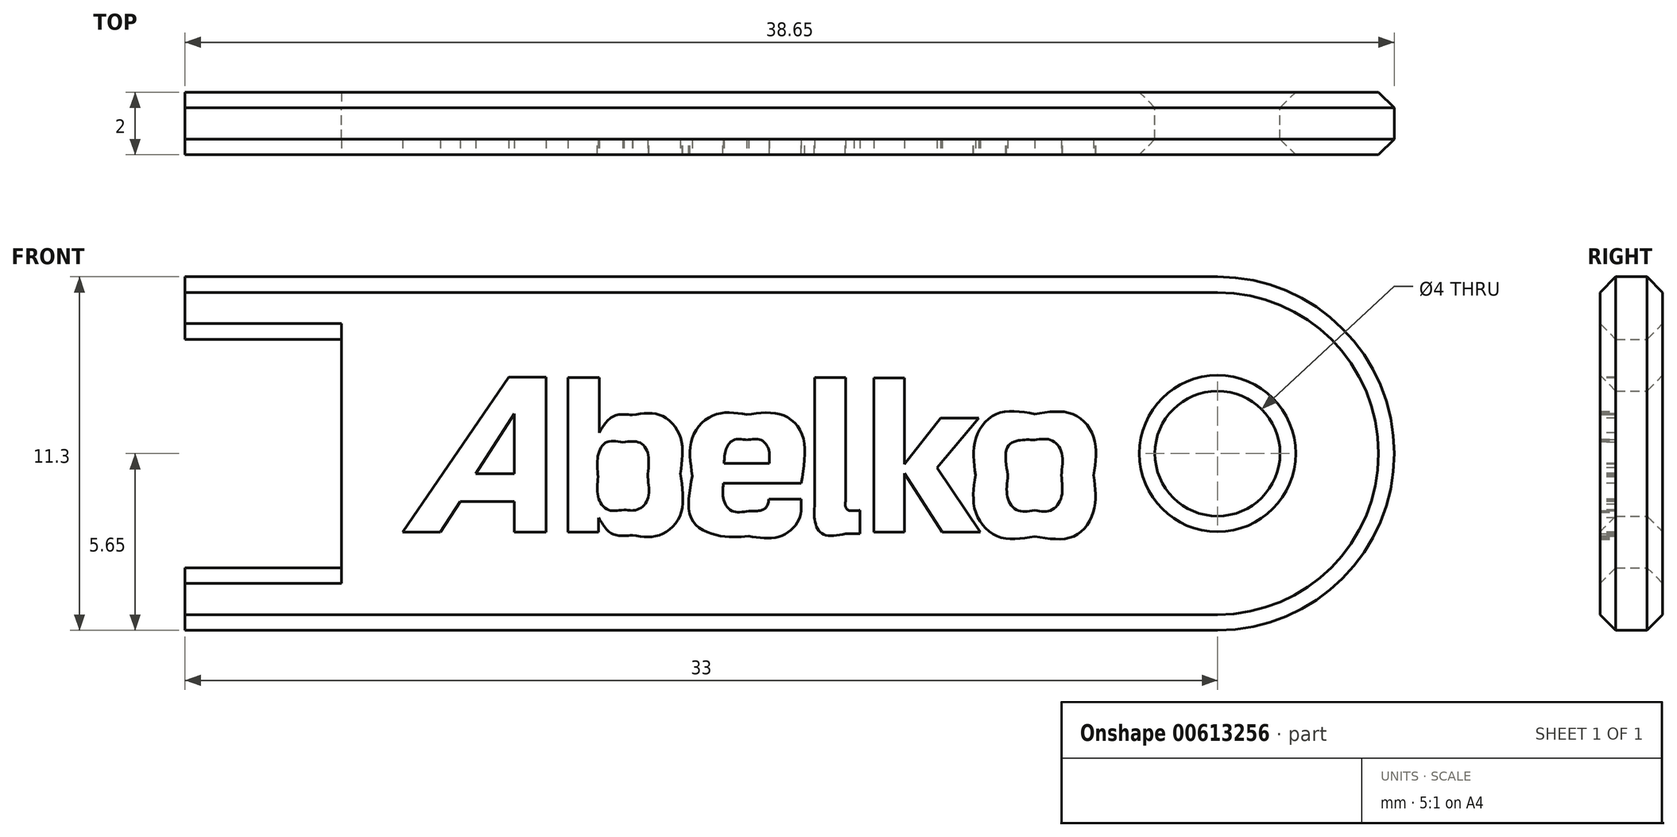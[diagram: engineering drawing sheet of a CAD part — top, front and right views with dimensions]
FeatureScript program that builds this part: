
annotation { "Feature Type Name" : "Feature", "Feature Type Description" : "" }
export const myFeature = defineFeature(function(context is Context, id is Id, definition is map)
    precondition{}
    {
        {
            var Q0;
            Q0=qCreatedBy(makeId("Front.planeOp"),FACE);
            var sketch = newSketch(context, id + "F0", { "sketchPlane" : qUnion([Q0])});
            skLineSegment(sketch, "E0", {"start": v(-13, 5.15) * mm, "end": v(-18, 5.15) * mm});
            skLineSegment(sketch, "E1", {"start": v(-18, 5.15) * mm, "end": v(-18, 7.15) * mm});
            skLineSegment(sketch, "E2", {"start": v(-18, 7.15) * mm, "end": v(15, 7.15) * mm});
            skLineSegment(sketch, "E3.MirrorCS", {"start": v(-18, -4.15) * mm, "end": v(15, -4.15) * mm});
            skLineSegment(sketch, "E4.MirrorCS", {"start": v(-18, -2.15) * mm, "end": v(-18, -4.15) * mm});
            skLineSegment(sketch, "E5.MirrorCS", {"start": v(-13, -2.15) * mm, "end": v(-18, -2.15) * mm});
            skArc(sketch, "E6", {"start": v(15, -4.15) * mm, "mid": v(20.65, 1.5) * mm, "end": v(15, 7.15) * mm});
            skLineSegment(sketch, "E7", {"start": v(-13, 5.15) * mm, "end": v(-13, -2.15) * mm});
            skLineSegment(sketch, "E8", {"start": v(-27.45, -20) * mm, "end": v(40.17, -20) * mm, "construction": true});
            skLineSegment(sketch, "E9", {"start": v(20.65, 1.5) * mm, "end": v(-13, 1.5) * mm, "construction": true});
            skCircle(sketch, "E10", {"center": v(15, 1.5) * mm, "radius": 2 * mm});
            skSolve(sketch);
        }
        {
            var Q0;
            Q0=makeQuery(id+"F0.imprint","IMPRINT",FACE,{"disambiguationData":[TD([[makeQuery(id+"F0.imprint","IMPRINT",EDGE,{"derivedFrom":sQuery(id+"F0.wireOp",EDGE,"akVr4v8H-JdDk-4HSe-9A5j-kgtD8AmrJHMh")}),-1.0]])]});
            var Q1;
            Q1=makeQuery(id+"F0.imprint","IMPRINT",FACE,{"disambiguationData":[TD([[makeQuery(id+"F0.imprint","IMPRINT",EDGE,{"derivedFrom":sQuery(id+"F0.wireOp",EDGE,"E0")}),-1.0]])]});
            extrude(context, id + "F1", {"entities" : qUnion([Q0, Q1]), "depth" : 2 * mm, "offsetDistance" : 25 * mm});
        }
        {
            var Q0;
            Q0=makeQuery(id+"F1.opExtrude","CAP_FACE",FACE,{"disambiguationData":[OSD([sQuery(id+"F0.wireOp",EDGE,"akVr4v8H-JdDk-4HSe-9A5j-kgtD8AmrJHMh"),sQuery(id+"F0.wireOp",EDGE,"E0"),sQuery(id+"F0.wireOp",EDGE,"E1"),sQuery(id+"F0.wireOp",EDGE,"E2"),sQuery(id+"F0.wireOp",EDGE,"ee2b3b4e-261e-4f05-bfb9-8a08e86599b6"),sQuery(id+"F0.wireOp",EDGE,"E3.MirrorCS"),sQuery(id+"F0.wireOp",EDGE,"26adf2fc-d08f-4d16-b653-455f8057de741.MirrorCS"),sQuery(id+"F0.wireOp",EDGE,"26adf2fc-d08f-4d16-b653-455f8057de742.MirrorCS"),sQuery(id+"F0.wireOp",EDGE,"E4.MirrorCS"),sQuery(id+"F0.wireOp",EDGE,"E5.MirrorCS")])],"isStart":false});
            var sketch = newSketch(context, id + "F2", { "sketchPlane" : qUnion([Q0])});
            skLineSegment(sketch, "E11", {"start": v(-8.71, 0.85) * mm, "end": v(-7.48, 0.85) * mm});
            skLineSegment(sketch, "E12", {"start": v(-7.48, 0.85) * mm, "end": v(-7.48, 2.77) * mm});
            skLineSegment(sketch, "E13", {"start": v(-7.48, 2.77) * mm, "end": v(-8.71, 0.85) * mm});
            skFitSpline(sketch, "E14", {"points": [v(-3.97, -0.3) * mm, v(-3.55, -0.3) * mm, v(-3.22, 0.04) * mm, v(-3.22, 0.75) * mm]});
            skFitSpline(sketch, "E15", {"points": [v(-3.22, 0.75) * mm, v(-3.22, 1.53) * mm, v(-3.5, 1.86) * mm, v(-4, 1.86) * mm]});
            skFitSpline(sketch, "E16", {"points": [v(-4, 1.86) * mm, v(-4.54, 1.86) * mm, v(-4.8, 1.45) * mm, v(-4.8, 0.76) * mm]});
            skFitSpline(sketch, "E17", {"points": [v(-4.8, 0.76) * mm, v(-4.8, 0.11) * mm, v(-4.49, -0.3) * mm, v(-3.97, -0.3) * mm]});
            skLineSegment(sketch, "E18", {"start": v(-6.46, 3.94) * mm, "end": v(-6.46, -1) * mm});
            skLineSegment(sketch, "E19", {"start": v(-6.46, -1) * mm, "end": v(-7.48, -1) * mm});
            skLineSegment(sketch, "E20", {"start": v(-7.48, -1) * mm, "end": v(-7.48, -0.04) * mm});
            skLineSegment(sketch, "E21", {"start": v(-7.48, -0.04) * mm, "end": v(-9.2, -0.04) * mm});
            skLineSegment(sketch, "E22", {"start": v(-9.2, -0.04) * mm, "end": v(-9.84, -1) * mm});
            skLineSegment(sketch, "E23", {"start": v(-9.84, -1) * mm, "end": v(-11.04, -1) * mm});
            skLineSegment(sketch, "E24", {"start": v(-11.04, -1) * mm, "end": v(-7.65, 3.94) * mm});
            skLineSegment(sketch, "E25", {"start": v(-7.65, 3.94) * mm, "end": v(-6.46, 3.94) * mm});
            skFitSpline(sketch, "E26", {"points": [v(-4.76, 2.17) * mm, v(-4.52, 2.52) * mm, v(-4.2, 2.73) * mm, v(-3.71, 2.73) * mm]});
            skFitSpline(sketch, "E27", {"points": [v(-3.71, 2.73) * mm, v(-2.82, 2.73) * mm, v(-2.17, 2.04) * mm, v(-2.17, 0.86) * mm]});
            skFitSpline(sketch, "E28", {"points": [v(-2.17, 0.86) * mm, v(-2.17, -0.47) * mm, v(-2.85, -1.11) * mm, v(-3.7, -1.11) * mm]});
            skFitSpline(sketch, "E29", {"points": [v(-3.7, -1.11) * mm, v(-4.2, -1.11) * mm, v(-4.48, -0.97) * mm, v(-4.78, -0.56) * mm]});
            skLineSegment(sketch, "E30", {"start": v(-4.76, 3.93) * mm, "end": v(-4.76, 2.17) * mm});
            skFitSpline(sketch, "E31", {"points": [v(0.67, 1.2) * mm, v(0.65, 1.64) * mm, v(0.4, 1.93) * mm, v(-0.05, 1.93) * mm]});
            skFitSpline(sketch, "E32", {"points": [v(-0.05, 1.93) * mm, v(-0.47, 1.93) * mm, v(-0.7, 1.65) * mm, v(-0.77, 1.2) * mm]});
            skLineSegment(sketch, "E33", {"start": v(-4.78, -0.56) * mm, "end": v(-4.78, -1.02) * mm});
            skLineSegment(sketch, "E34", {"start": v(-4.78, -1.02) * mm, "end": v(-5.76, -1.02) * mm});
            skLineSegment(sketch, "E35", {"start": v(-5.76, -1.02) * mm, "end": v(-5.76, 3.93) * mm});
            skLineSegment(sketch, "E36", {"start": v(-5.76, 3.93) * mm, "end": v(-4.76, 3.93) * mm});
            skFitSpline(sketch, "E37", {"points": [v(-0.05, 2.74) * mm, v(1.05, 2.74) * mm, v(1.74, 2.08) * mm, v(1.7, 0.54) * mm]});
            skLineSegment(sketch, "E38", {"start": v(-0.77, 1.2) * mm, "end": v(0.67, 1.2) * mm});
            skFitSpline(sketch, "E39", {"points": [v(-0.8, 0.54) * mm, v(-0.79, 0.04) * mm, v(-0.52, -0.34) * mm, v(0.02, -0.34) * mm]});
            skFitSpline(sketch, "E40", {"points": [v(0.02, -0.34) * mm, v(0.27, -0.34) * mm, v(0.55, -0.25) * mm, v(0.66, 0.04) * mm]});
            skLineSegment(sketch, "E41", {"start": v(1.7, 0.54) * mm, "end": v(-0.8, 0.54) * mm});
            skFitSpline(sketch, "E42", {"points": [v(1.69, 0.04) * mm, v(1.63, -0.6) * mm, v(1.03, -1.14) * mm, v(0, -1.14) * mm]});
            skFitSpline(sketch, "E43", {"points": [v(0, -1.14) * mm, v(-0.84, -1.14) * mm, v(-1.79, -0.64) * mm, v(-1.79, 0.78) * mm]});
            skFitSpline(sketch, "E44", {"points": [v(-1.79, 0.78) * mm, v(-1.79, 2.02) * mm, v(-1.06, 2.74) * mm, v(-0.05, 2.74) * mm]});
            skFitSpline(sketch, "E45", {"points": [v(3.38, -0.32) * mm, v(3.44, -0.32) * mm, v(3.53, -0.32) * mm, v(3.57, -0.32) * mm]});
            skLineSegment(sketch, "E46", {"start": v(0.66, 0.04) * mm, "end": v(1.69, 0.04) * mm});
            skFitSpline(sketch, "E47", {"points": [v(3.57, -1.06) * mm, v(3.42, -1.06) * mm, v(3.27, -1.06) * mm, v(3.12, -1.06) * mm]});
            skFitSpline(sketch, "E48", {"points": [v(3.12, -1.06) * mm, v(2.37, -1.06) * mm, v(2.12, -0.62) * mm, v(2.12, -0.12) * mm]});
            skLineSegment(sketch, "E49", {"start": v(3.57, -0.32) * mm, "end": v(3.57, -1.06) * mm});
            skFitSpline(sketch, "E50", {"points": [v(3.12, 0.02) * mm, v(3.12, -0.21) * mm, v(3.22, -0.32) * mm, v(3.38, -0.32) * mm]});
            skLineSegment(sketch, "E51", {"start": v(2.12, -0.12) * mm, "end": v(2.12, 3.93) * mm});
            skLineSegment(sketch, "E52", {"start": v(2.12, 3.93) * mm, "end": v(3.12, 3.93) * mm});
            skLineSegment(sketch, "E53", {"start": v(3.12, 3.93) * mm, "end": v(3.12, 0.02) * mm});
            skFitSpline(sketch, "E54", {"points": [v(9.15, -0.32) * mm, v(9.68, -0.32) * mm, v(10, 0.1) * mm, v(10, 0.8) * mm]});
            skFitSpline(sketch, "E55", {"points": [v(10, 0.8) * mm, v(10, 1.56) * mm, v(9.66, 1.93) * mm, v(9.15, 1.93) * mm]});
            skFitSpline(sketch, "E56", {"points": [v(9.15, 1.93) * mm, v(8.75, 1.93) * mm, v(8.3, 1.73) * mm, v(8.3, 0.81) * mm]});
            skFitSpline(sketch, "E57", {"points": [v(8.3, 0.81) * mm, v(8.3, 0.06) * mm, v(8.62, -0.32) * mm, v(9.15, -0.32) * mm]});
            skLineSegment(sketch, "E58", {"start": v(4.99, 3.91) * mm, "end": v(4.99, 1.16) * mm});
            skLineSegment(sketch, "E59", {"start": v(4.99, 1.16) * mm, "end": v(6.15, 2.63) * mm});
            skLineSegment(sketch, "E60", {"start": v(6.15, 2.63) * mm, "end": v(7.37, 2.63) * mm});
            skLineSegment(sketch, "E61", {"start": v(7.37, 2.63) * mm, "end": v(6.04, 1.04) * mm});
            skLineSegment(sketch, "E62", {"start": v(6.04, 1.04) * mm, "end": v(7.42, -1.02) * mm});
            skLineSegment(sketch, "E63", {"start": v(7.42, -1.02) * mm, "end": v(6.2, -1.02) * mm});
            skLineSegment(sketch, "E64", {"start": v(6.2, -1.02) * mm, "end": v(4.99, 0.87) * mm});
            skLineSegment(sketch, "E65", {"start": v(4.99, 0.87) * mm, "end": v(4.99, -1.02) * mm});
            skLineSegment(sketch, "E66", {"start": v(4.99, -1.02) * mm, "end": v(4.01, -1.02) * mm});
            skLineSegment(sketch, "E67", {"start": v(4.01, -1.02) * mm, "end": v(4.01, 3.91) * mm});
            skLineSegment(sketch, "E68", {"start": v(4.01, 3.91) * mm, "end": v(4.99, 3.91) * mm});
            skFitSpline(sketch, "E69", {"points": [v(9.15, 2.77) * mm, v(10.36, 2.77) * mm, v(11.04, 2) * mm, v(11.04, 0.8) * mm]});
            skFitSpline(sketch, "E70", {"points": [v(11.04, 0.8) * mm, v(11.04, -0.32) * mm, v(10.4, -1.15) * mm, v(9.16, -1.15) * mm]});
            skFitSpline(sketch, "E71", {"points": [v(9.16, -1.15) * mm, v(7.97, -1.15) * mm, v(7.26, -0.35) * mm, v(7.26, 0.81) * mm]});
            skFitSpline(sketch, "E72", {"points": [v(7.26, 0.81) * mm, v(7.26, 1.94) * mm, v(7.93, 2.77) * mm, v(9.15, 2.77) * mm]});
            skLineSegment(sketch, "E73", {"start": v(-6, -3.9) * mm, "end": v(-5.71, -3.9) * mm});
            skLineSegment(sketch, "E74", {"start": v(-5.71, -3.9) * mm, "end": v(-5.71, -2.37) * mm});
            skLineSegment(sketch, "E75", {"start": v(-5.71, -2.37) * mm, "end": v(-6, -2.37) * mm});
            skLineSegment(sketch, "E76", {"start": v(-6, -2.37) * mm, "end": v(-6, -3.9) * mm});
            skLineSegment(sketch, "E77", {"start": v(-4.47, -2.37) * mm, "end": v(-4.19, -2.37) * mm});
            skLineSegment(sketch, "E78", {"start": v(-4.19, -2.37) * mm, "end": v(-4.19, -3.9) * mm});
            skLineSegment(sketch, "E79", {"start": v(-4.19, -3.9) * mm, "end": v(-4.44, -3.9) * mm});
            skLineSegment(sketch, "E80", {"start": v(-4.44, -3.9) * mm, "end": v(-5.11, -2.83) * mm});
            skLineSegment(sketch, "E81", {"start": v(-5.11, -2.83) * mm, "end": v(-5.1, -3.9) * mm});
            skLineSegment(sketch, "E82", {"start": v(-5.1, -3.9) * mm, "end": v(-5.38, -3.9) * mm});
            skLineSegment(sketch, "E83", {"start": v(-5.38, -3.9) * mm, "end": v(-5.38, -2.37) * mm});
            skLineSegment(sketch, "E84", {"start": v(-5.38, -2.37) * mm, "end": v(-5.12, -2.37) * mm});
            skLineSegment(sketch, "E85", {"start": v(-5.12, -2.37) * mm, "end": v(-4.44, -3.45) * mm});
            skLineSegment(sketch, "E86", {"start": v(-4.44, -3.45) * mm, "end": v(-4.47, -2.37) * mm});
            skFitSpline(sketch, "E87", {"points": [v(-1.65, -2.6) * mm, v(-1.92, -2.6) * mm, v(-2.1, -2.8) * mm, v(-2.1, -3.12) * mm]});
            skFitSpline(sketch, "E88", {"points": [v(-2.1, -3.12) * mm, v(-2.1, -3.47) * mm, v(-1.9, -3.68) * mm, v(-1.65, -3.68) * mm]});
            skFitSpline(sketch, "E89", {"points": [v(-1.65, -3.68) * mm, v(-1.45, -3.68) * mm, v(-1.2, -3.54) * mm, v(-1.2, -3.17) * mm]});
            skFitSpline(sketch, "E90", {"points": [v(-1.2, -3.17) * mm, v(-1.2, -2.87) * mm, v(-1.35, -2.6) * mm, v(-1.65, -2.6) * mm]});
            skLineSegment(sketch, "E91", {"start": v(-2.94, -2.37) * mm, "end": v(-2.66, -2.37) * mm});
            skLineSegment(sketch, "E92", {"start": v(-2.66, -2.37) * mm, "end": v(-2.66, -3.9) * mm});
            skLineSegment(sketch, "E93", {"start": v(-2.66, -3.9) * mm, "end": v(-2.9, -3.9) * mm});
            skLineSegment(sketch, "E94", {"start": v(-2.9, -3.9) * mm, "end": v(-3.58, -2.83) * mm});
            skLineSegment(sketch, "E95", {"start": v(-3.58, -2.83) * mm, "end": v(-3.56, -3.9) * mm});
            skLineSegment(sketch, "E96", {"start": v(-3.56, -3.9) * mm, "end": v(-3.85, -3.9) * mm});
            skLineSegment(sketch, "E97", {"start": v(-3.85, -3.9) * mm, "end": v(-3.85, -2.37) * mm});
            skLineSegment(sketch, "E98", {"start": v(-3.85, -2.37) * mm, "end": v(-3.59, -2.37) * mm});
            skLineSegment(sketch, "E99", {"start": v(-3.59, -2.37) * mm, "end": v(-2.9, -3.45) * mm});
            skLineSegment(sketch, "E100", {"start": v(-2.9, -3.45) * mm, "end": v(-2.94, -2.37) * mm});
            skFitSpline(sketch, "E101", {"points": [v(-1.65, -3.94) * mm, v(-1.85, -3.94) * mm, v(-2.03, -3.89) * mm, v(-2.18, -3.7) * mm]});
            skFitSpline(sketch, "E102", {"points": [v(-2.18, -3.7) * mm, v(-2.34, -3.53) * mm, v(-2.39, -3.33) * mm, v(-2.39, -3.14) * mm]});
            skFitSpline(sketch, "E103", {"points": [v(-2.39, -3.14) * mm, v(-2.39, -2.67) * mm, v(-2.07, -2.33) * mm, v(-1.65, -2.33) * mm]});
            skFitSpline(sketch, "E104", {"points": [v(-1.65, -2.33) * mm, v(-1.27, -2.33) * mm, v(-0.91, -2.61) * mm, v(-0.91, -3.14) * mm]});
            skFitSpline(sketch, "E105", {"points": [v(-0.91, -3.14) * mm, v(-0.92, -3.58) * mm, v(-1.18, -3.94) * mm, v(-1.65, -3.94) * mm]});
            skLineSegment(sketch, "E106", {"start": v(0.44, -2.37) * mm, "end": v(0, -3.9) * mm});
            skLineSegment(sketch, "E107", {"start": v(0, -3.9) * mm, "end": v(-0.39, -3.9) * mm});
            skLineSegment(sketch, "E108", {"start": v(-0.39, -3.9) * mm, "end": v(-0.84, -2.37) * mm});
            skLineSegment(sketch, "E109", {"start": v(-0.84, -2.37) * mm, "end": v(-0.54, -2.37) * mm});
            skLineSegment(sketch, "E110", {"start": v(-0.54, -2.37) * mm, "end": v(-0.2, -3.58) * mm});
            skLineSegment(sketch, "E111", {"start": v(-0.2, -3.58) * mm, "end": v(0.14, -2.37) * mm});
            skLineSegment(sketch, "E112", {"start": v(0.14, -2.37) * mm, "end": v(0.44, -2.37) * mm});
            skLineSegment(sketch, "E113", {"start": v(1.28, -3.35) * mm, "end": v(1.07, -2.65) * mm});
            skLineSegment(sketch, "E114", {"start": v(1.07, -2.65) * mm, "end": v(0.86, -3.35) * mm});
            skLineSegment(sketch, "E115", {"start": v(0.86, -3.35) * mm, "end": v(1.28, -3.35) * mm});
            skLineSegment(sketch, "E116", {"start": v(1.36, -3.6) * mm, "end": v(0.78, -3.6) * mm});
            skLineSegment(sketch, "E117", {"start": v(0.78, -3.6) * mm, "end": v(0.7, -3.9) * mm});
            skLineSegment(sketch, "E118", {"start": v(0.7, -3.9) * mm, "end": v(0.38, -3.9) * mm});
            skLineSegment(sketch, "E119", {"start": v(0.38, -3.9) * mm, "end": v(0.9, -2.37) * mm});
            skLineSegment(sketch, "E120", {"start": v(0.9, -2.37) * mm, "end": v(1.23, -2.37) * mm});
            skLineSegment(sketch, "E121", {"start": v(1.23, -2.37) * mm, "end": v(1.75, -3.9) * mm});
            skLineSegment(sketch, "E122", {"start": v(1.75, -3.9) * mm, "end": v(1.45, -3.9) * mm});
            skLineSegment(sketch, "E123", {"start": v(1.45, -3.9) * mm, "end": v(1.36, -3.6) * mm});
            skLineSegment(sketch, "E124", {"start": v(2.78, -2.63) * mm, "end": v(2.35, -2.63) * mm});
            skLineSegment(sketch, "E125", {"start": v(2.35, -2.63) * mm, "end": v(2.35, -3.9) * mm});
            skLineSegment(sketch, "E126", {"start": v(2.35, -3.9) * mm, "end": v(2.06, -3.9) * mm});
            skLineSegment(sketch, "E127", {"start": v(2.06, -3.9) * mm, "end": v(2.06, -2.63) * mm});
            skLineSegment(sketch, "E128", {"start": v(2.06, -2.63) * mm, "end": v(1.65, -2.63) * mm});
            skLineSegment(sketch, "E129", {"start": v(1.65, -2.63) * mm, "end": v(1.65, -2.37) * mm});
            skLineSegment(sketch, "E130", {"start": v(1.65, -2.37) * mm, "end": v(2.78, -2.37) * mm});
            skLineSegment(sketch, "E131", {"start": v(2.78, -2.37) * mm, "end": v(2.78, -2.63) * mm});
            skFitSpline(sketch, "E132", {"points": [v(4.29, -2.6) * mm, v(4.02, -2.6) * mm, v(3.85, -2.8) * mm, v(3.85, -3.12) * mm]});
            skFitSpline(sketch, "E133", {"points": [v(3.85, -3.12) * mm, v(3.85, -3.47) * mm, v(4.04, -3.68) * mm, v(4.3, -3.68) * mm]});
            skFitSpline(sketch, "E134", {"points": [v(4.3, -3.68) * mm, v(4.49, -3.68) * mm, v(4.73, -3.54) * mm, v(4.74, -3.17) * mm]});
            skFitSpline(sketch, "E135", {"points": [v(4.74, -3.17) * mm, v(4.74, -2.87) * mm, v(4.59, -2.6) * mm, v(4.29, -2.6) * mm]});
            skLineSegment(sketch, "E136", {"start": v(3, -3.9) * mm, "end": v(3.28, -3.9) * mm});
            skLineSegment(sketch, "E137", {"start": v(3.28, -3.9) * mm, "end": v(3.28, -2.37) * mm});
            skLineSegment(sketch, "E138", {"start": v(3.28, -2.37) * mm, "end": v(3, -2.37) * mm});
            skLineSegment(sketch, "E139", {"start": v(3, -2.37) * mm, "end": v(3, -3.9) * mm});
            skFitSpline(sketch, "E140", {"points": [v(4.29, -3.94) * mm, v(4.1, -3.94) * mm, v(3.91, -3.89) * mm, v(3.76, -3.7) * mm]});
            skFitSpline(sketch, "E141", {"points": [v(3.76, -3.7) * mm, v(3.6, -3.53) * mm, v(3.55, -3.33) * mm, v(3.55, -3.14) * mm]});
            skFitSpline(sketch, "E142", {"points": [v(3.55, -3.14) * mm, v(3.55, -2.67) * mm, v(3.87, -2.33) * mm, v(4.29, -2.33) * mm]});
            skFitSpline(sketch, "E143", {"points": [v(4.29, -2.33) * mm, v(4.67, -2.33) * mm, v(5.03, -2.61) * mm, v(5.03, -3.14) * mm]});
            skFitSpline(sketch, "E144", {"points": [v(5.03, -3.14) * mm, v(5.02, -3.58) * mm, v(4.76, -3.94) * mm, v(4.29, -3.94) * mm]});
            skLineSegment(sketch, "E145", {"start": v(6.19, -2.37) * mm, "end": v(6.47, -2.37) * mm});
            skLineSegment(sketch, "E146", {"start": v(6.47, -2.37) * mm, "end": v(6.47, -3.9) * mm});
            skLineSegment(sketch, "E147", {"start": v(6.47, -3.9) * mm, "end": v(6.22, -3.9) * mm});
            skLineSegment(sketch, "E148", {"start": v(6.22, -3.9) * mm, "end": v(5.55, -2.83) * mm});
            skLineSegment(sketch, "E149", {"start": v(5.55, -2.83) * mm, "end": v(5.56, -3.9) * mm});
            skLineSegment(sketch, "E150", {"start": v(5.56, -3.9) * mm, "end": v(5.28, -3.9) * mm});
            skLineSegment(sketch, "E151", {"start": v(5.28, -3.9) * mm, "end": v(5.28, -2.37) * mm});
            skLineSegment(sketch, "E152", {"start": v(5.28, -2.37) * mm, "end": v(5.54, -2.37) * mm});
            skLineSegment(sketch, "E153", {"start": v(5.54, -2.37) * mm, "end": v(6.22, -3.45) * mm});
            skLineSegment(sketch, "E154", {"start": v(6.22, -3.45) * mm, "end": v(6.19, -2.37) * mm});
            skLineSegment(sketch, "E155", {"start": v(-6.46, 1.47) * mm, "end": v(12.06, 1.47) * mm, "construction": true});
            skSolve(sketch);
        }
        {
            var Q0;
            Q0=makeQuery(id+"F2.imprint","IMPRINT",FACE,{"disambiguationData":[TD([[makeQuery(id+"F2.imprint","IMPRINT",EDGE,{"derivedFrom":sQuery(id+"F2.wireOp",EDGE,"E11")}),-1.0]])]});
            var Q1;
            Q1=makeQuery(id+"F2.imprint","IMPRINT",FACE,{"disambiguationData":[TD([[makeQuery(id+"F2.imprint","IMPRINT",EDGE,{"derivedFrom":sQuery(id+"F2.wireOp",EDGE,"E14")}),-1.0]])]});
            var Q2;
            Q2=makeQuery(id+"F2.imprint","IMPRINT",FACE,{"disambiguationData":[TD([[makeQuery(id+"F2.imprint","IMPRINT",EDGE,{"derivedFrom":sQuery(id+"F2.wireOp",EDGE,"E31")}),-1.0]])]});
            var Q3;
            Q3=makeQuery(id+"F2.imprint","IMPRINT",FACE,{"disambiguationData":[TD([[makeQuery(id+"F2.imprint","IMPRINT",EDGE,{"derivedFrom":sQuery(id+"F2.wireOp",EDGE,"E45")}),-1.0]])]});
            var Q4;
            Q4=makeQuery(id+"F2.imprint","IMPRINT",FACE,{"disambiguationData":[TD([[makeQuery(id+"F2.imprint","IMPRINT",EDGE,{"derivedFrom":sQuery(id+"F2.wireOp",EDGE,"E58")}),-1.0]])]});
            var Q5;
            Q5=makeQuery(id+"F2.imprint","IMPRINT",FACE,{"disambiguationData":[TD([[makeQuery(id+"F2.imprint","IMPRINT",EDGE,{"derivedFrom":sQuery(id+"F2.wireOp",EDGE,"E54")}),-1.0]])]});
            extrude(context, id + "F3", {"entities" : qUnion([Q0, Q1, Q2, Q3, Q4, Q5]), "operationType" : NewBodyOperationType.REMOVE, "oppositeDirection" : true, "depth" : 0.5 * mm, "offsetDistance" : 25 * mm});
        }
        {
            var Q0;
            Q0=makeQuery(id+"F1.opExtrude","SWEPT_FACE",FACE,{"disambiguationData":[OSD([sQuery(id+"F0.wireOp",EDGE,"E1")])]});
            var sketch = newSketch(context, id + "F4", { "sketchPlane" : qUnion([Q0])});
            skLineSegment(sketch, "E156", {"start": v(0, 5.65) * mm, "end": v(0, 6.65) * mm});
            skLineSegment(sketch, "E157", {"start": v(0, 6.65) * mm, "end": v(0.5, 7.15) * mm});
            skLineSegment(sketch, "E158", {"start": v(0.5, 7.15) * mm, "end": v(1.5, 7.15) * mm});
            skLineSegment(sketch, "E159", {"start": v(1.5, 7.15) * mm, "end": v(2, 6.65) * mm});
            skLineSegment(sketch, "E160", {"start": v(2, 6.65) * mm, "end": v(2, 5.65) * mm});
            skLineSegment(sketch, "E161", {"start": v(2, 5.65) * mm, "end": v(1.5, 5.15) * mm});
            skLineSegment(sketch, "E162", {"start": v(1.5, 5.15) * mm, "end": v(0.5, 5.15) * mm});
            skLineSegment(sketch, "E163", {"start": v(0.5, 5.15) * mm, "end": v(0, 5.65) * mm});
            skSolve(sketch);
        }
        {
            var Q0;
            Q0=makeQuery(id+"F1.opExtrude","SWEPT_FACE",FACE,{"disambiguationData":[OSD([sQuery(id+"F0.wireOp",EDGE,"E4.MirrorCS")])]});
            var sketch = newSketch(context, id + "F5", { "sketchPlane" : qUnion([Q0])});
            skLineSegment(sketch, "E164", {"start": v(0, -3.65) * mm, "end": v(0, -2.65) * mm});
            skLineSegment(sketch, "E165", {"start": v(0, -2.65) * mm, "end": v(0.5, -2.15) * mm});
            skLineSegment(sketch, "E166", {"start": v(0.5, -2.15) * mm, "end": v(1.5, -2.15) * mm});
            skLineSegment(sketch, "E167", {"start": v(1.5, -2.15) * mm, "end": v(2, -2.65) * mm});
            skLineSegment(sketch, "E168", {"start": v(2, -2.65) * mm, "end": v(2, -3.65) * mm});
            skLineSegment(sketch, "E169", {"start": v(2, -3.65) * mm, "end": v(1.5, -4.15) * mm});
            skLineSegment(sketch, "E170", {"start": v(1.5, -4.15) * mm, "end": v(0.5, -4.15) * mm});
            skLineSegment(sketch, "E171", {"start": v(0.5, -4.15) * mm, "end": v(0, -3.65) * mm});
            skSolve(sketch);
        }
        {
            var Q0;
            {var subQ0=sQuery(id+"F4.wireOp",EDGE,"E163");Q0=makeQuery(id+"F4.imprint","IMPRINT",FACE,{"disambiguationData":[TD([[makeQuery(id+"F4.imprint","IMPRINT",EDGE,{"derivedFrom":subQ0}),1.0]])]});}
            var Q1;
            {var subQ0=sQuery(id+"F4.wireOp",EDGE,"E157");Q1=makeQuery(id+"F4.imprint","IMPRINT",FACE,{"disambiguationData":[TD([[makeQuery(id+"F4.imprint","IMPRINT",EDGE,{"derivedFrom":subQ0}),1.0]])]});}
            var Q2;
            {var subQ0=sQuery(id+"F4.wireOp",EDGE,"E159");Q2=makeQuery(id+"F4.imprint","IMPRINT",FACE,{"disambiguationData":[TD([[makeQuery(id+"F4.imprint","IMPRINT",EDGE,{"derivedFrom":subQ0}),1.0]])]});}
            var Q3;
            {var subQ0=sQuery(id+"F4.wireOp",EDGE,"E161");Q3=makeQuery(id+"F4.imprint","IMPRINT",FACE,{"disambiguationData":[TD([[makeQuery(id+"F4.imprint","IMPRINT",EDGE,{"derivedFrom":subQ0}),1.0]])]});}
            var Q4;
            {var subQ0=sQuery(id+"F5.wireOp",EDGE,"E165");Q4=makeQuery(id+"F5.imprint","IMPRINT",FACE,{"disambiguationData":[TD([[makeQuery(id+"F5.imprint","IMPRINT",EDGE,{"derivedFrom":subQ0}),1.0]])]});}
            var Q5;
            {var subQ0=sQuery(id+"F5.wireOp",EDGE,"E167");Q5=makeQuery(id+"F5.imprint","IMPRINT",FACE,{"disambiguationData":[TD([[makeQuery(id+"F5.imprint","IMPRINT",EDGE,{"derivedFrom":subQ0}),1.0]])]});}
            var Q6;
            {var subQ0=sQuery(id+"F5.wireOp",EDGE,"E169");Q6=makeQuery(id+"F5.imprint","IMPRINT",FACE,{"disambiguationData":[TD([[makeQuery(id+"F5.imprint","IMPRINT",EDGE,{"derivedFrom":subQ0}),1.0]])]});}
            var Q7;
            {var subQ0=sQuery(id+"F5.wireOp",EDGE,"E171");Q7=makeQuery(id+"F5.imprint","IMPRINT",FACE,{"disambiguationData":[TD([[makeQuery(id+"F5.imprint","IMPRINT",EDGE,{"derivedFrom":subQ0}),1.0]])]});}
            extrude(context, id + "F6", {"entities" : qUnion([Q0, Q1, Q2, Q3, Q4, Q5, Q6, Q7]), "operationType" : NewBodyOperationType.REMOVE, "oppositeDirection" : true, "depth" : 5 * mm, "offsetDistance" : 25 * mm});
        }
        {
            var Q0;
            Q0=makeQuery(id+"F1.opExtrude","CAP_EDGE",EDGE,{"disambiguationData":[OSD([sQuery(id+"F0.wireOp",EDGE,"E3.MirrorCS")])],"isStart":false});
            var Q1;
            Q1=makeQuery(id+"F1.opExtrude","CAP_EDGE",EDGE,{"disambiguationData":[OSD([sQuery(id+"F0.wireOp",EDGE,"E6")])],"isStart":false});
            var Q2;
            Q2=makeQuery(id+"F1.opExtrude","CAP_EDGE",EDGE,{"disambiguationData":[OSD([sQuery(id+"F0.wireOp",EDGE,"E2")])],"isStart":false});
            var Q3;
            Q3=makeQuery(id+"F1.opExtrude","CAP_EDGE",EDGE,{"disambiguationData":[OSD([sQuery(id+"F0.wireOp",EDGE,"E3.MirrorCS")])],"isStart":true});
            var Q4;
            Q4=makeQuery(id+"F1.opExtrude","CAP_EDGE",EDGE,{"disambiguationData":[OSD([sQuery(id+"F0.wireOp",EDGE,"E10")])],"isStart":false});
            var Q5;
            Q5=makeQuery(id+"F1.opExtrude","CAP_EDGE",EDGE,{"disambiguationData":[OSD([sQuery(id+"F0.wireOp",EDGE,"E10")])],"isStart":true});
            chamfer(context, id + "F7", {"entities" : qUnion([Q0, Q1, Q2, Q3, Q4, Q5]), "width" : 0.5 * mm, "tangentPropagation" : true});
        }
    });
